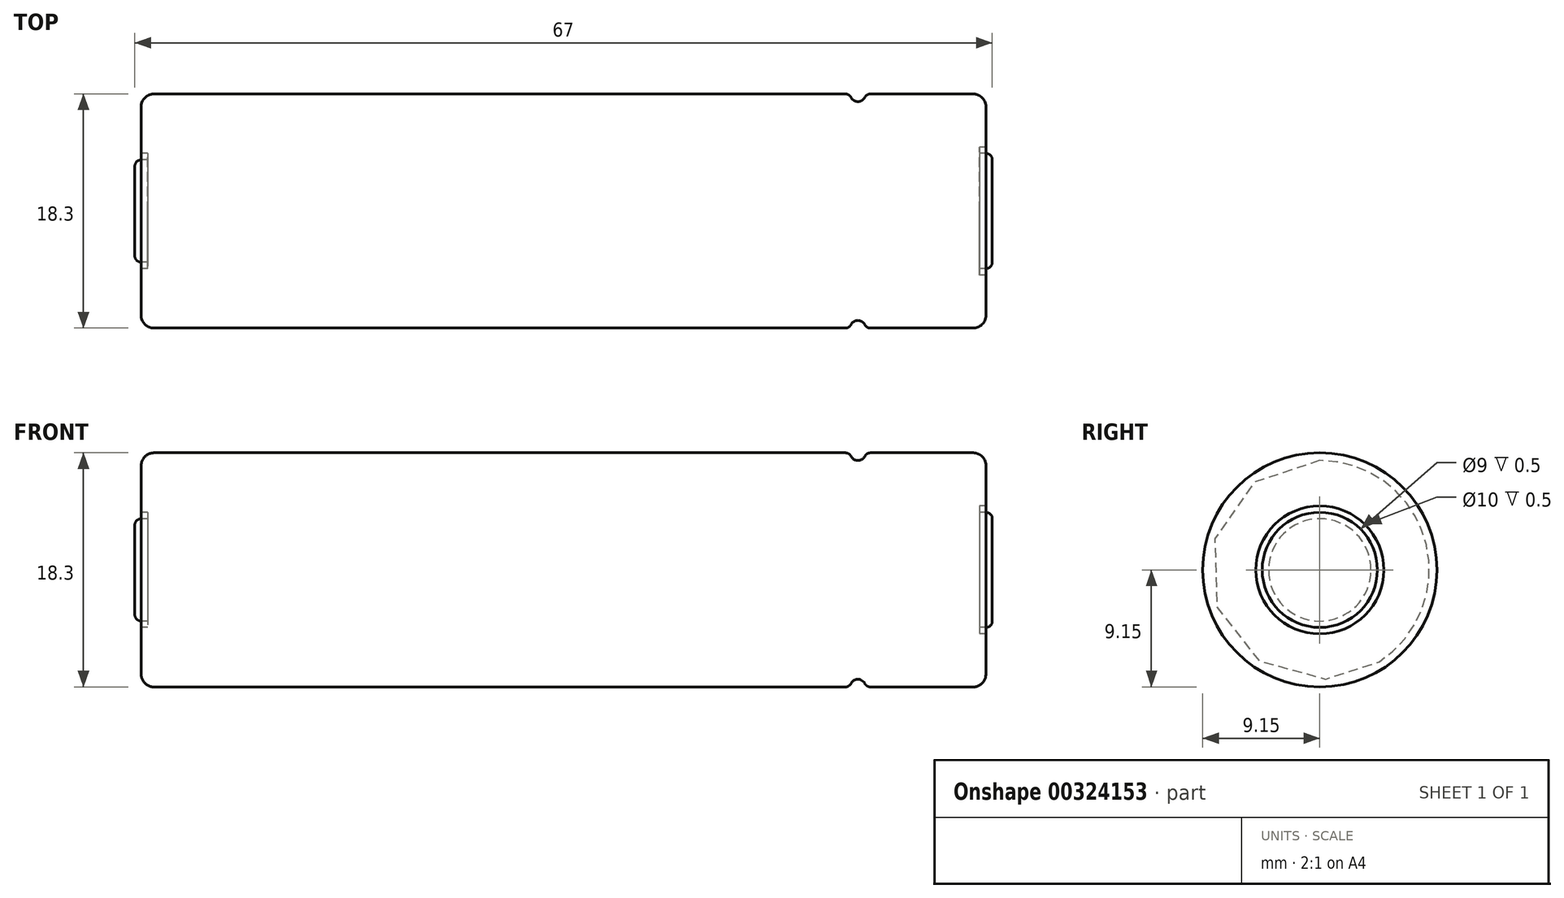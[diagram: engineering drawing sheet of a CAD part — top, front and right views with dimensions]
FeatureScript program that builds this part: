
annotation { "Feature Type Name" : "Feature", "Feature Type Description" : "" }
export const myFeature = defineFeature(function(context is Context, id is Id, definition is map)
    precondition{}
    {
        {
            var Q0;
            Q0=qCreatedBy(makeId("Front.planeOp"),FACE);
            var sketch = newSketch(context, id + "F0", { "sketchPlane" : qUnion([Q0])});
            skLineSegment(sketch, "E0", {"start": v(0, 0) * mm, "end": v(0, 4) * mm});
            skLineSegment(sketch, "E1", {"start": v(0, 4) * mm, "end": v(1, 4) * mm});
            skLineSegment(sketch, "E2", {"start": v(0.5, 9.15) * mm, "end": v(55.9, 9.15) * mm});
            skLineSegment(sketch, "E3", {"start": v(66.5, 9.15) * mm, "end": v(66.5, 5) * mm});
            skLineSegment(sketch, "E4", {"start": v(66.5, 5) * mm, "end": v(66, 5) * mm});
            skLineSegment(sketch, "E5", {"start": v(66, 5) * mm, "end": v(66, 4.5) * mm});
            skLineSegment(sketch, "E6", {"start": v(66, 4.5) * mm, "end": v(67, 4.5) * mm});
            skLineSegment(sketch, "E7", {"start": v(67, 4.5) * mm, "end": v(67, 0) * mm});
            skLineSegment(sketch, "E8", {"start": v(67, 0) * mm, "end": v(0, 0) * mm, "construction": true});
            skLineSegment(sketch, "E9", {"start": v(1, 4) * mm, "end": v(1, 4.5) * mm});
            skLineSegment(sketch, "E10", {"start": v(1, 4.5) * mm, "end": v(0.5, 4.5) * mm});
            skLineSegment(sketch, "E11", {"start": v(0.5, 4.5) * mm, "end": v(0.5, 9.15) * mm});
            skArc(sketch, "E12", {"start": v(55.9, 9.15) * mm, "mid": v(56.5, 8.55) * mm, "end": v(57.1, 9.15) * mm});
            skLineSegment(sketch, "E13.trimOffspring", {"start": v(57.1, 9.15) * mm, "end": v(66.5, 9.15) * mm});
            skSolve(sketch);
        }
        {
            var Q0;
            Q0 = qConstructionFilter(qBodyType(qCreatedBy(id + "F0" ,EDGE), BodyType.WIRE), ConstructionObject.NO);
            var Q1;
            Q1=sQuery(id+"F0.wireOp",EDGE,"E8");
            revolve(context, id + "F1", {"bodyType" : ToolBodyType.SURFACE, "operationType" : NewBodyOperationType.ADD, "surfaceEntities" : qUnion([Q0]), "axis" : qUnion([Q1]), "revolveType" : RevolveType.FULL});
        }
        {
            var Q0;
            Q0=makeQuery(id+"F1.opRevolve","SWEPT_EDGE",EDGE,{"disambiguationData":[OSD([sQuery(id+"F0.wireOp",VERTEX,"E13.trimOffspring.end")])]});
            var Q1;
            Q1=makeQuery(id+"F1.opRevolve","SWEPT_EDGE",EDGE,{"disambiguationData":[OSD([sQuery(id+"F0.wireOp",VERTEX,"E11.end")])]});
            fillet(context, id + "F2", {"entities" : qUnion([Q0, Q1]), "radius" : 1 * mm, "tangentPropagation" : true, "allowEdgeOverflow" : false});
        }
        {
            var Q0;
            Q0=makeQuery(id+"F1.opRevolve","SWEPT_EDGE",EDGE,{"disambiguationData":[OSD([sQuery(id+"F0.wireOp",VERTEX,"E13.trimOffspring.start")])]});
            var Q1;
            Q1=makeQuery(id+"F1.opRevolve","SWEPT_EDGE",EDGE,{"disambiguationData":[OSD([sQuery(id+"F0.wireOp",VERTEX,"E12.start")])]});
            fillet(context, id + "F3", {"entities" : qUnion([Q0, Q1]), "radius" : .5 * mm, "tangentPropagation" : true, "allowEdgeOverflow" : false});
        }
        {
            var Q0;
            Q0=makeQuery(id+"F1.opRevolve","SWEPT_FACE",FACE,{"disambiguationData":[OSD([sQuery(id+"F0.wireOp",EDGE,"E7")])]});
            var Q1;
            Q1=makeQuery(id+"F1.opRevolve","SWEPT_FACE",FACE,{"disambiguationData":[OSD([sQuery(id+"F0.wireOp",EDGE,"E0")])]});
            fillet(context, id + "F4", {"entities" : qUnion([Q0, Q1]), "radius" : .5 * mm, "tangentPropagation" : true, "allowEdgeOverflow" : false});
        }
    });
